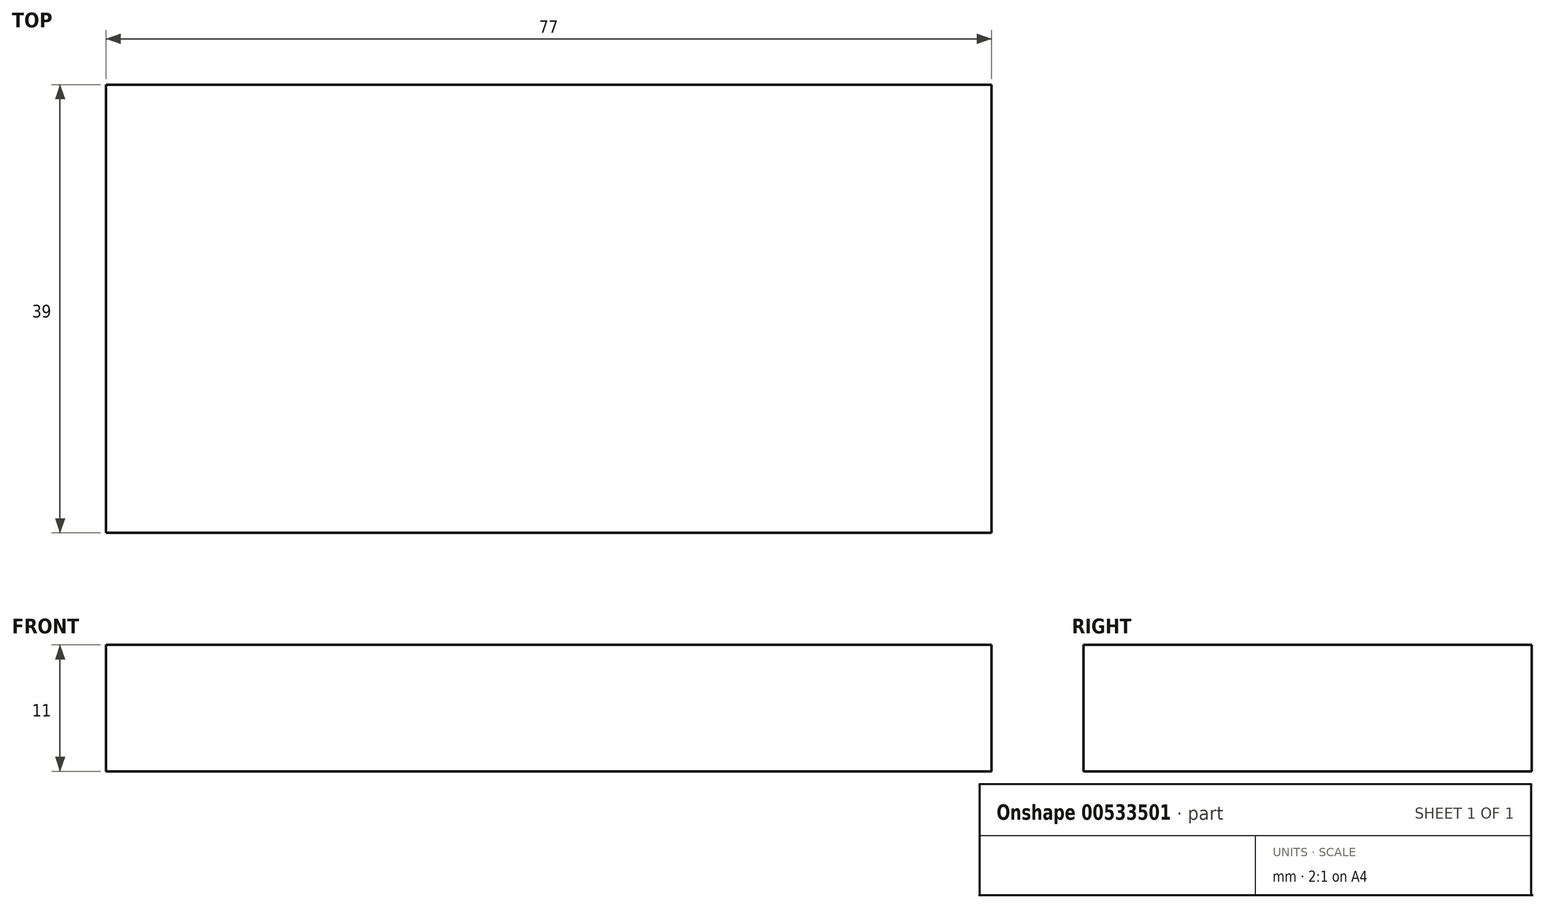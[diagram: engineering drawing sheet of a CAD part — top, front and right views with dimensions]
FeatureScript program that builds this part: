
annotation { "Feature Type Name" : "Feature", "Feature Type Description" : "" }
export const myFeature = defineFeature(function(context is Context, id is Id, definition is map)
    precondition{}
    {
        {
            var Q0;
            Q0=qCreatedBy(makeId("Top.planeOp"),FACE);
            var sketch = newSketch(context, id + "F0", { "sketchPlane" : qUnion([Q0])});
            skLineSegment(sketch, "E0.bottom", {"start": v(0, 0) * mm, "end": v(77, 0) * mm});
            skLineSegment(sketch, "E0.top", {"start": v(0, 39) * mm, "end": v(77, 39) * mm});
            skLineSegment(sketch, "E0.left", {"start": v(0, 0) * mm, "end": v(0, 39) * mm});
            skLineSegment(sketch, "E0.right", {"start": v(77, 0) * mm, "end": v(77, 39) * mm});
            skSolve(sketch);
        }
        {
            var Q0;
            Q0=qSketchRegion(id+"F0",true);
            extrude(context, id + "F1", {"entities" : qUnion([Q0]), "depth" : 11 * mm, "offsetDistance" : 25 * mm});
        }
    });
